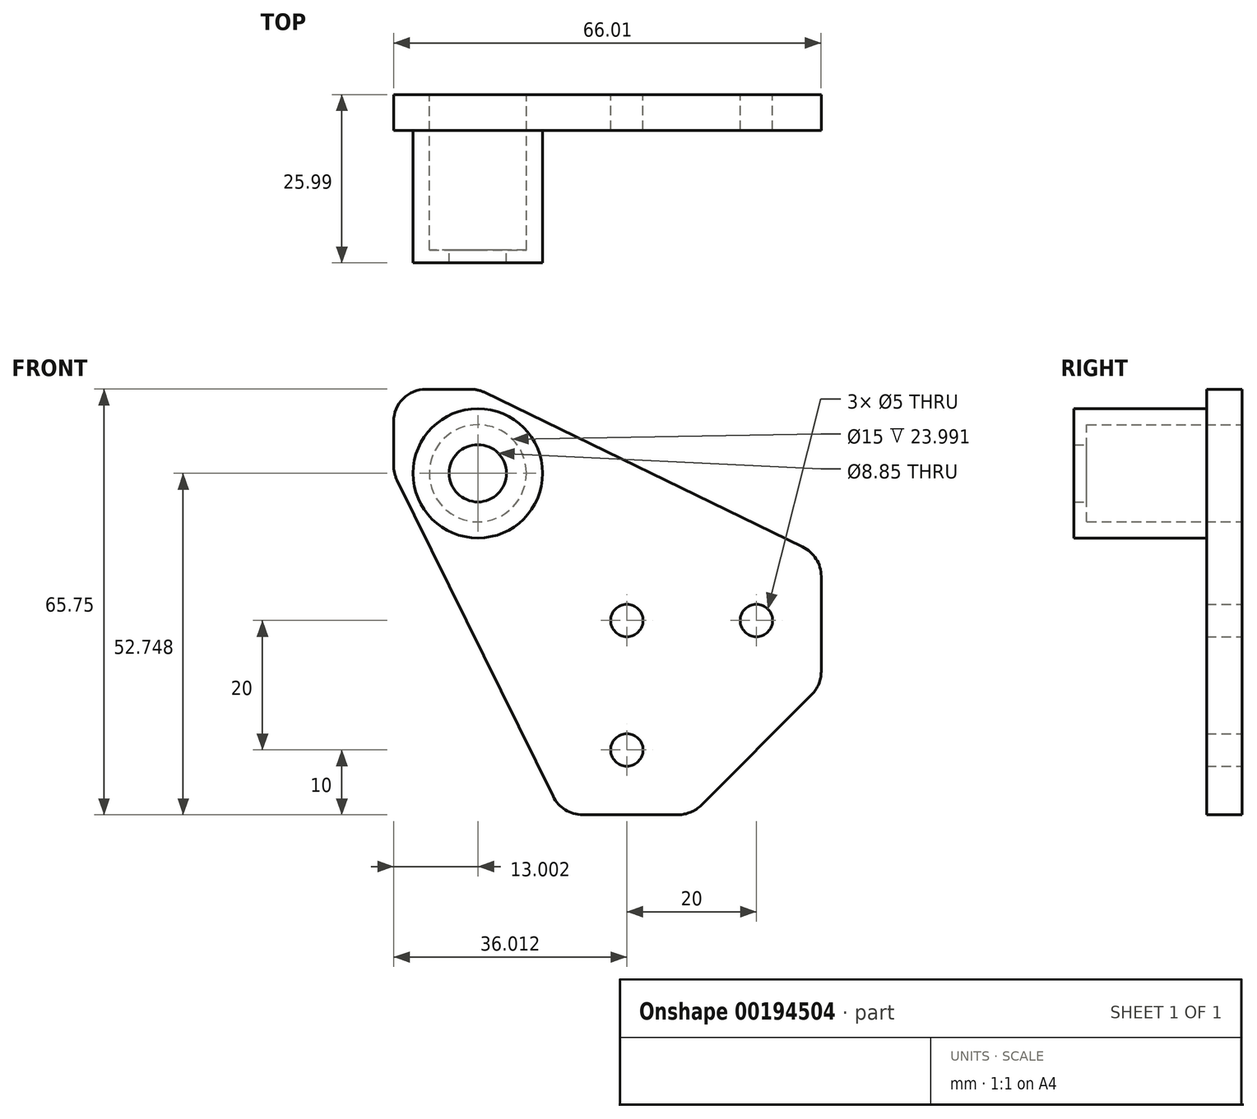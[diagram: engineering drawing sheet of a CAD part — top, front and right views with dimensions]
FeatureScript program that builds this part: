
annotation { "Feature Type Name" : "Feature", "Feature Type Description" : "" }
export const myFeature = defineFeature(function(context is Context, id is Id, definition is map)
    precondition{}
    {
        {
            var Q0;
            Q0=qCreatedBy(makeId("Front.planeOp"),FACE);
            var sketch = newSketch(context, id + "F0", { "sketchPlane" : qUnion([Q0])});
            skLineSegment(sketch, "E0.top", {"start": v(-11.66, -20) * mm, "end": v(1.27, -20) * mm});
            skLineSegment(sketch, "E1.right", {"start": v(23.34, 15) * mm, "end": v(23.34, 2.07) * mm});
            skLineSegment(sketch, "E2", {"start": v(4.8, -18.54) * mm, "end": v(21.88, -1.46) * mm});
            skPoint(sketch, "E3.visualSharp", {"position": v(-16.66, 20) * mm});
            skPoint(sketch, "E4.visualSharp", {"position": v(-16.66, -20) * mm});
            skPoint(sketch, "E5.visualSharp", {"position": v(23.34, 20) * mm});
            skPoint(sketch, "E6.visualSharp", {"position": v(23.34, 0) * mm});
            skArc(sketch, "E6.filletArc", {"start": v(21.88, -1.46) * mm, "mid": v(22.96, 0.16) * mm, "end": v(23.34, 2.07) * mm});
            skPoint(sketch, "E7.visualSharp", {"position": v(3.34, -20) * mm});
            skArc(sketch, "E7.filletArc", {"start": v(1.27, -20) * mm, "mid": v(3.18, -19.62) * mm, "end": v(4.8, -18.54) * mm});
            skPoint(sketch, "E8", {"position": v(-5.2, -20) * mm});
            skPoint(sketch, "E9", {"position": v(23.34, 8.54) * mm});
            skPoint(sketch, "E10", {"position": v(-6.66, 0) * mm});
            skPoint(sketch, "E11", {"position": v(3.34, 10) * mm});
            skPoint(sketch, "E12", {"position": v(-6.66, 20) * mm});
            skPoint(sketch, "E13", {"position": v(-16.66, 10) * mm});
            skCircle(sketch, "E14", {"center": v(-6.66, 10) * mm, "radius": 2.5 * mm});
            skCircle(sketch, "E15", {"center": v(13.34, 10) * mm, "radius": 2.5 * mm});
            skCircle(sketch, "E16", {"center": v(-6.66, -10) * mm, "radius": 2.5 * mm});
            skCircle(sketch, "E17", {"center": v(-29.67, 32.75) * mm, "radius": 7.5 * mm});
            skLineSegment(sketch, "E18", {"start": v(-16.66, -20) * mm, "end": v(-11.66, -20) * mm});
            skLineSegment(sketch, "E19", {"start": v(23.34, 20) * mm, "end": v(23.34, 15) * mm});
            skLineSegment(sketch, "E20", {"start": v(-42.67, 33.91) * mm, "end": v(-42.67, 40.75) * mm});
            skLineSegment(sketch, "E21", {"start": v(-37.67, 45.75) * mm, "end": v(-30.82, 45.75) * mm});
            skLineSegment(sketch, "E22", {"start": v(-28.63, 45.25) * mm, "end": v(23.34, 20) * mm});
            skLineSegment(sketch, "E23", {"start": v(-42.15, 31.7) * mm, "end": v(-16.66, -20) * mm});
            skPoint(sketch, "E24.visualSharp", {"position": v(-42.67, 45.75) * mm});
            skArc(sketch, "E24.filletArc", {"start": v(-37.67, 45.75) * mm, "mid": v(-41.2, 44.28) * mm, "end": v(-42.67, 40.75) * mm});
            skPoint(sketch, "E25.visualSharp", {"position": v(-29.67, 45.75) * mm});
            skArc(sketch, "E25.filletArc", {"start": v(-28.63, 45.25) * mm, "mid": v(-29.7, 45.62) * mm, "end": v(-30.82, 45.75) * mm});
            skPoint(sketch, "E26.visualSharp", {"position": v(-42.67, 32.75) * mm});
            skArc(sketch, "E26.filletArc", {"start": v(-42.67, 33.91) * mm, "mid": v(-42.54, 32.78) * mm, "end": v(-42.15, 31.7) * mm});
            skSolve(sketch);
        }
        {
            var Q0;
            Q0=makeQuery(id+"F0.imprint","IMPRINT",FACE,{"disambiguationData":[TD([[makeQuery(id+"F0.imprint","IMPRINT",EDGE,{"derivedFrom":sQuery(id+"F0.wireOp",EDGE,"E0.top")}),1.0]])]});
            extrude(context, id + "F1", {"entities" : qUnion([Q0]), "depth" : 5.5 * mm, "offsetDistance" : 25.4 * mm});
        }
        {
            var Q0;
            Q0=makeQuery(id+"F1.opExtrude","SWEPT_EDGE",EDGE,{"disambiguationData":[OSD([sQuery(id+"F0.wireOp",EDGE,"E18"),sQuery(id+"F0.wireOp",EDGE,"E23")])]});
            var Q1;
            Q1=makeQuery(id+"F1.opExtrude","SWEPT_EDGE",EDGE,{"disambiguationData":[OSD([sQuery(id+"F0.wireOp",EDGE,"E19"),sQuery(id+"F0.wireOp",EDGE,"E22")])]});
            fillet(context, id + "F2", {"entities" : qUnion([Q0, Q1]), "radius" : 5.08 * mm, "tangentPropagation" : true, "allowEdgeOverflow" : false});
        }
        {
            var Q0;
            Q0=makeQuery(id+"F1.opExtrude","CAP_FACE",FACE,{"disambiguationData":[OSD([sQuery(id+"F0.wireOp",EDGE,"E0.top"),sQuery(id+"F0.wireOp",EDGE,"E1.right"),sQuery(id+"F0.wireOp",EDGE,"E2"),sQuery(id+"F0.wireOp",EDGE,"E6.filletArc"),sQuery(id+"F0.wireOp",EDGE,"E7.filletArc"),sQuery(id+"F0.wireOp",EDGE,"E14"),sQuery(id+"F0.wireOp",EDGE,"E15"),sQuery(id+"F0.wireOp",EDGE,"E16"),sQuery(id+"F0.wireOp",EDGE,"E18"),sQuery(id+"F0.wireOp",EDGE,"E19"),sQuery(id+"F0.wireOp",EDGE,"E20"),sQuery(id+"F0.wireOp",EDGE,"E21"),sQuery(id+"F0.wireOp",EDGE,"E22"),sQuery(id+"F0.wireOp",EDGE,"E23"),sQuery(id+"F0.wireOp",EDGE,"E24.filletArc"),sQuery(id+"F0.wireOp",EDGE,"E25.filletArc"),sQuery(id+"F0.wireOp",EDGE,"E26.filletArc"),sQuery(id+"F0.wireOp",EDGE,"E17")])],"isStart":false});
            var sketch = newSketch(context, id + "F3", { "sketchPlane" : qUnion([Q0])});
            skCircle(sketch, "E27", {"center": v(-29.67, 32.75) * mm, "radius": 7.5 * mm});
            skCircle(sketch, "E28", {"center": v(-29.67, 32.75) * mm, "radius": 10 * mm});
            skSolve(sketch);
        }
        {
            var Q0;
            Q0 = qSketchRegion(id + "F3", true);
            extrude(context, id + "F4", {"entities" : qUnion([Q0]), "operationType" : NewBodyOperationType.ADD, "depth" : 18.5 * mm, "offsetDistance" : 25.4 * mm});
        }
        {
            var Q0;
            Q0=makeQuery(id+"F4.opExtrude","CAP_FACE",FACE,{"disambiguationData":[OSD([sQuery(id+"F3.wireOp",EDGE,"E27"),sQuery(id+"F3.wireOp",EDGE,"E28")])],"isStart":false});
            var sketch = newSketch(context, id + "F5", { "sketchPlane" : qUnion([Q0])});
            skCircle(sketch, "E29", {"center": v(-29.67, 32.75) * mm, "radius": 10 * mm});
            skPoint(sketch, "E29.first.point", {"position": v(-36, 40.48) * mm});
            skPoint(sketch, "E29.second.point", {"position": v(-23.33, 25.01) * mm});
            skPoint(sketch, "E29.third.point", {"position": v(-22.78, 25.5) * mm});
            skCircle(sketch, "E30", {"center": v(-29.67, 32.75) * mm, "radius": 4.43 * mm});
            skSolve(sketch);
        }
        {
            var Q0;
            Q0 = qSketchRegion(id + "F5", true);
            extrude(context, id + "F6", {"entities" : qUnion([Q0]), "operationType" : NewBodyOperationType.ADD, "depth" : 2 * mm, "offsetDistance" : 25.4 * mm});
        }
    });
